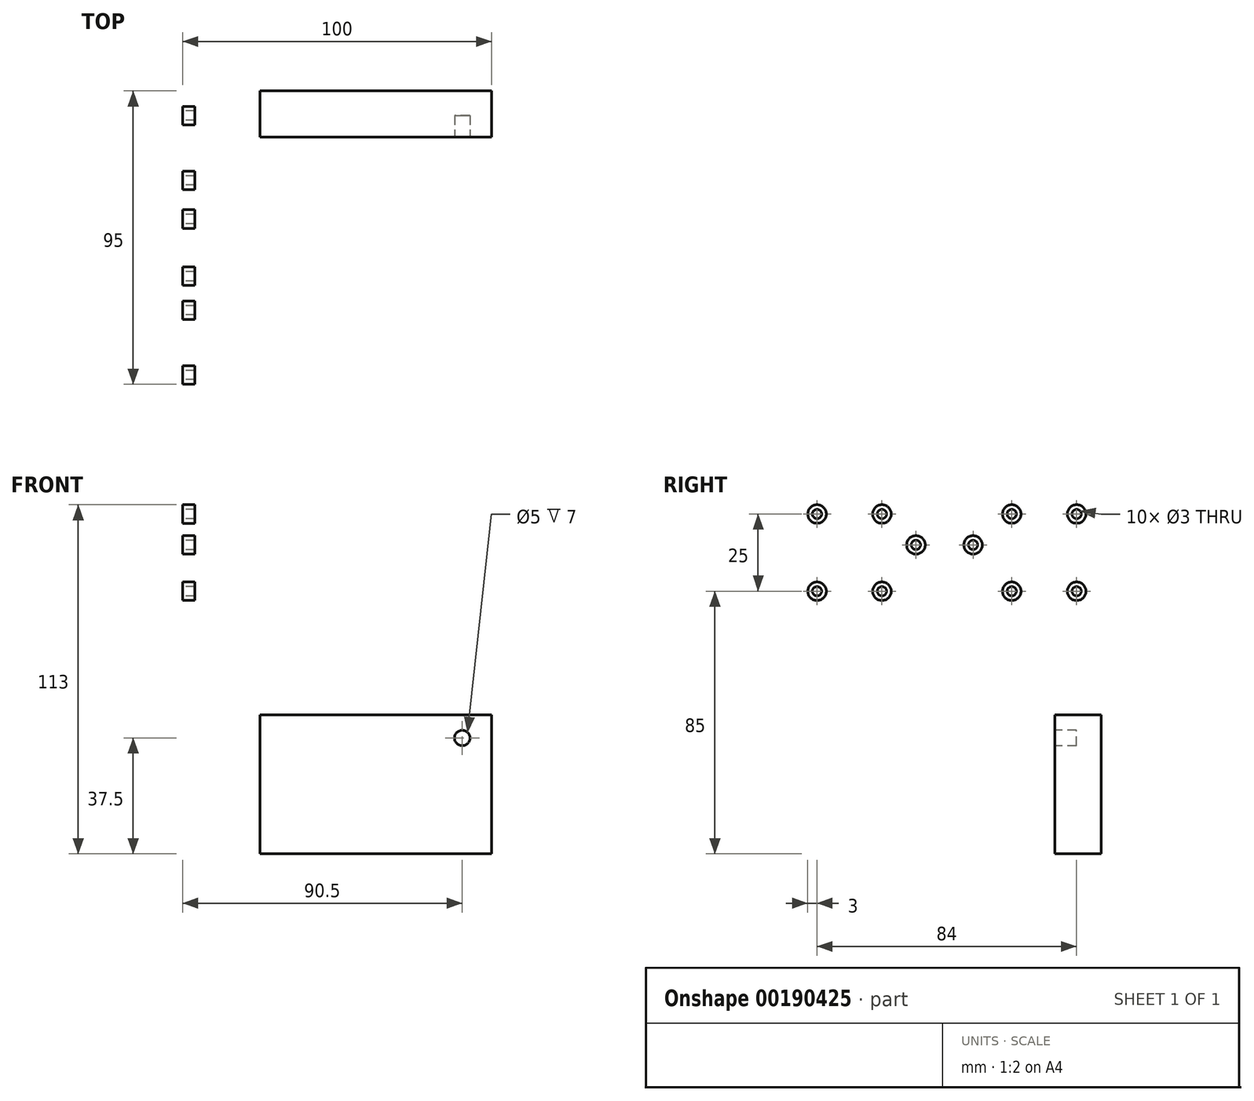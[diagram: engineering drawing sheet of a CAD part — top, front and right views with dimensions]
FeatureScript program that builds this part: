
annotation { "Feature Type Name" : "Feature", "Feature Type Description" : "" }
export const myFeature = defineFeature(function(context is Context, id is Id, definition is map)
    precondition{}
    {
        {
            var Q0;
            Q0=qCreatedBy(makeId("Top.planeOp"),FACE);
            var sketch = newSketch(context, id + "F0", { "sketchPlane" : qUnion([Q0])});
            skLineSegment(sketch, "E0.bottom", {"start": v(0, 0) * mm, "end": v(700, 0) * mm, "construction": true});
            skLineSegment(sketch, "E0.top", {"start": v(0, 670) * mm, "end": v(700, 670) * mm, "construction": true});
            skLineSegment(sketch, "E0.left", {"start": v(0, 0) * mm, "end": v(0, 670) * mm, "construction": true});
            skLineSegment(sketch, "E0.right", {"start": v(700, 0) * mm, "end": v(700, 670) * mm, "construction": true});
            skLineSegment(sketch, "E1.bottom", {"start": v(50, 50) * mm, "end": v(158, 50) * mm, "construction": true});
            skLineSegment(sketch, "E1.top", {"start": v(50, 150) * mm, "end": v(158, 150) * mm, "construction": true});
            skLineSegment(sketch, "E1.left", {"start": v(50, 50) * mm, "end": v(50, 150) * mm, "construction": true});
            skLineSegment(sketch, "E1.right", {"start": v(158, 50) * mm, "end": v(158, 150) * mm, "construction": true});
            skSolve(sketch);
        }
        {
            var Q0;
            Q0=qCreatedBy(makeId("Top.planeOp"),FACE);
            var sketch = newSketch(context, id + "F1", { "sketchPlane" : qUnion([Q0])});
            skLineSegment(sketch, "E2.bottom", {"start": v(50, 150) * mm, "end": v(158, 150) * mm});
            skLineSegment(sketch, "E2.top", {"start": v(50, 50) * mm, "end": v(158, 50) * mm});
            skLineSegment(sketch, "E2.left", {"start": v(50, 150) * mm, "end": v(50, 50) * mm});
            skLineSegment(sketch, "E2.right", {"start": v(158, 150) * mm, "end": v(158, 50) * mm});
            skCircle(sketch, "E3", {"center": v(104.5, 100) * mm, "radius": 21.5 * mm});
            skPoint(sketch, "E4", {"position": v(158, 100) * mm});
            skLineSegment(sketch, "E5.bottom", {"start": v(158, 99.75) * mm, "end": v(126, 99.75) * mm});
            skLineSegment(sketch, "E5.top", {"start": v(158, 100.25) * mm, "end": v(126, 100.25) * mm});
            skLineSegment(sketch, "E5.left", {"start": v(158, 100.25) * mm, "end": v(158, 99.75) * mm});
            skLineSegment(sketch, "E5.right", {"start": v(126, 100.25) * mm, "end": v(126, 99.75) * mm});
            skPoint(sketch, "E6", {"position": v(126, 100) * mm});
            skLineSegment(sketch, "E7.bottom", {"start": v(126, 100.25) * mm, "end": v(100.94, 100.25) * mm});
            skLineSegment(sketch, "E7.top", {"start": v(126, 99.75) * mm, "end": v(100.94, 99.75) * mm});
            skLineSegment(sketch, "E7.right", {"start": v(100.94, 100.25) * mm, "end": v(100.94, 99.75) * mm});
            skLineSegment(sketch, "E8.bottom", {"start": v(158, 150) * mm, "end": v(83, 150) * mm});
            skLineSegment(sketch, "E8.top", {"start": v(158, 135) * mm, "end": v(83, 135) * mm});
            skLineSegment(sketch, "E8.left", {"start": v(158, 150) * mm, "end": v(158, 135) * mm});
            skLineSegment(sketch, "E8.right", {"start": v(83, 150) * mm, "end": v(83, 135) * mm});
            skLineSegment(sketch, "E9.bottom", {"start": v(158, 50) * mm, "end": v(83, 50) * mm});
            skLineSegment(sketch, "E9.top", {"start": v(158, 65) * mm, "end": v(83, 65) * mm});
            skLineSegment(sketch, "E9.left", {"start": v(158, 50) * mm, "end": v(158, 65) * mm});
            skLineSegment(sketch, "E9.right", {"start": v(83, 50) * mm, "end": v(83, 65) * mm});
            skSolve(sketch);
        }
        {
            var Q0;
            Q0=qCreatedBy(makeId("Front.planeOp"),FACE);
            var sketch = newSketch(context, id + "F2", { "sketchPlane" : qUnion([Q0])});
            skPoint(sketch, "E10", {"position": v(158, 0) * mm});
            skPoint(sketch, "E11", {"position": v(50, 0) * mm});
            skLineSegment(sketch, "E12.bottom", {"start": v(50, 30) * mm, "end": v(158, 30) * mm});
            skLineSegment(sketch, "E12.top", {"start": v(50, 45) * mm, "end": v(158, 45) * mm});
            skLineSegment(sketch, "E12.left", {"start": v(50, 30) * mm, "end": v(50, 45) * mm});
            skLineSegment(sketch, "E12.right", {"start": v(158, 30) * mm, "end": v(158, 45) * mm});
            skLineSegment(sketch, "E13.bottom", {"start": v(50, 45) * mm, "end": v(58, 45) * mm});
            skLineSegment(sketch, "E13.top", {"start": v(50, 225) * mm, "end": v(58, 225) * mm});
            skLineSegment(sketch, "E13.left", {"start": v(50, 45) * mm, "end": v(50, 225) * mm});
            skLineSegment(sketch, "E13.right", {"start": v(58, 45) * mm, "end": v(58, 225) * mm});
            skLineSegment(sketch, "E14.bottom", {"start": v(158, 30) * mm, "end": v(50, 30) * mm});
            skLineSegment(sketch, "E14.top", {"start": v(158, 0) * mm, "end": v(50, 0) * mm});
            skLineSegment(sketch, "E14.left", {"start": v(158, 30) * mm, "end": v(158, 0) * mm});
            skLineSegment(sketch, "E14.right", {"start": v(50, 30) * mm, "end": v(50, 0) * mm});
            skLineSegment(sketch, "E15.bottom", {"start": v(50, 225) * mm, "end": v(158, 225) * mm, "construction": true});
            skLineSegment(sketch, "E15.left", {"start": v(50, 225) * mm, "end": v(50, 45) * mm});
            skLineSegment(sketch, "E15.right", {"start": v(158, 225) * mm, "end": v(158, 45) * mm});
            skLineSegment(sketch, "E16.bottom", {"start": v(50, 225) * mm, "end": v(158, 225) * mm});
            skLineSegment(sketch, "E16.top", {"start": v(50, 295) * mm, "end": v(158, 295) * mm});
            skLineSegment(sketch, "E16.left", {"start": v(50, 225) * mm, "end": v(50, 295) * mm});
            skLineSegment(sketch, "E16.right", {"start": v(158, 225) * mm, "end": v(158, 295) * mm});
            skCircle(sketch, "E17", {"center": v(148.5, 37.5) * mm, "radius": 2.5 * mm});
            skPoint(sketch, "E18", {"position": v(158, 37.5) * mm});
            skSolve(sketch);
        }
        {
            var Q0;
            {var subQ1=sQuery(id+"F1.wireOp",EDGE,"E2.bottom");Q0=makeQuery(id+"F1.imprint","IMPRINT",FACE,{"disambiguationData":[TD([[makeQuery(id+"F1.imprint","IMPRINT",EDGE,{"derivedFrom":subQ1}),-1.0]])]});}
            extrude(context, id + "F3", {"entities" : qUnion([Q0]), "depth" : 230 * mm});
        }
        {
            var Q0;
            Q0=makeQuery(id+"F2.imprint","IMPRINT",FACE,{"disambiguationData":[TD([[makeQuery(id+"F2.imprint","IMPRINT",EDGE,{"derivedFrom":sQuery(id+"F2.wireOp",EDGE,"E14.bottom")}),1.0]])]});
            var Q1;
            {var subQ0=sQuery(id+"F2.wireOp",EDGE,"E13.right");Q1=makeQuery(id+"F2.imprint","IMPRINT",FACE,{"disambiguationData":[TD([[makeQuery(id+"F2.imprint","IMPRINT",EDGE,{"derivedFrom":subQ0}),-1.0]])]});}
            var Q2;
            Q2=makeQuery(id+"F2.imprint","IMPRINT",FACE,{"disambiguationData":[TD([[makeQuery(id+"F2.imprint","IMPRINT",EDGE,{"derivedFrom":sQuery(id+"F2.wireOp",EDGE,"E16.top")}),-1.0]])]});
            extrude(context, id + "F4", {"entities" : qUnion([Q0, Q1, Q2]), "operationType" : NewBodyOperationType.REMOVE, "oppositeDirection" : true, "depth" : 310 * mm});
        }
        {
            var Q0;
            Q0=qCreatedBy(makeId("Right.planeOp"),FACE);
            var sketch = newSketch(context, id + "F5", { "sketchPlane" : qUnion([Q0])});
            skCircle(sketch, "E19", {"center": v(142, 85) * mm, "radius": 1.5 * mm});
            skCircle(sketch, "E20", {"center": v(58, 85) * mm, "radius": 1.5 * mm});
            skCircle(sketch, "E21", {"center": v(142, 110) * mm, "radius": 1.5 * mm});
            skCircle(sketch, "E22", {"center": v(58, 110) * mm, "radius": 1.5 * mm});
            skCircle(sketch, "E23", {"center": v(121, 110) * mm, "radius": 1.5 * mm});
            skCircle(sketch, "E24", {"center": v(121, 85) * mm, "radius": 1.5 * mm});
            skCircle(sketch, "E25", {"center": v(79, 110) * mm, "radius": 1.5 * mm});
            skCircle(sketch, "E26", {"center": v(79, 85) * mm, "radius": 1.5 * mm});
            skCircle(sketch, "E27", {"center": v(108.5, 100) * mm, "radius": 1.5 * mm});
            skCircle(sketch, "E28", {"center": v(90, 100) * mm, "radius": 1.5 * mm});
            skCircle(sketch, "E29", {"center": v(58, 110) * mm, "radius": 3 * mm});
            skCircle(sketch, "E30", {"center": v(79, 110) * mm, "radius": 3 * mm});
            skCircle(sketch, "E31", {"center": v(90, 100) * mm, "radius": 3 * mm});
            skCircle(sketch, "E32", {"center": v(108.5, 100) * mm, "radius": 3 * mm});
            skCircle(sketch, "E33", {"center": v(121, 110) * mm, "radius": 3 * mm});
            skCircle(sketch, "E34", {"center": v(142, 110) * mm, "radius": 3 * mm});
            skCircle(sketch, "E35", {"center": v(121, 85) * mm, "radius": 3 * mm});
            skCircle(sketch, "E36", {"center": v(142, 85) * mm, "radius": 3 * mm});
            skCircle(sketch, "E37", {"center": v(79, 85) * mm, "radius": 3 * mm});
            skCircle(sketch, "E38", {"center": v(58, 85) * mm, "radius": 3 * mm});
            skSolve(sketch);
        }
        {
            var Q0;
            Q0=makeQuery(id+"F5.imprint","IMPRINT",FACE,{"disambiguationData":[TD([[makeQuery(id+"F5.imprint","IMPRINT",EDGE,{"derivedFrom":sQuery(id+"F5.wireOp",EDGE,"E19")}),1.0]])]});
            var Q1;
            Q1=makeQuery(id+"F5.imprint","IMPRINT",FACE,{"disambiguationData":[TD([[makeQuery(id+"F5.imprint","IMPRINT",EDGE,{"derivedFrom":sQuery(id+"F5.wireOp",EDGE,"E21")}),1.0]])]});
            var Q2;
            Q2=makeQuery(id+"F5.imprint","IMPRINT",FACE,{"disambiguationData":[TD([[makeQuery(id+"F5.imprint","IMPRINT",EDGE,{"derivedFrom":sQuery(id+"F5.wireOp",EDGE,"E23")}),1.0]])]});
            var Q3;
            Q3=makeQuery(id+"F5.imprint","IMPRINT",FACE,{"disambiguationData":[TD([[makeQuery(id+"F5.imprint","IMPRINT",EDGE,{"derivedFrom":sQuery(id+"F5.wireOp",EDGE,"E27")}),1.0]])]});
            var Q4;
            Q4=makeQuery(id+"F5.imprint","IMPRINT",FACE,{"disambiguationData":[TD([[makeQuery(id+"F5.imprint","IMPRINT",EDGE,{"derivedFrom":sQuery(id+"F5.wireOp",EDGE,"E24")}),1.0]])]});
            var Q5;
            Q5=makeQuery(id+"F5.imprint","IMPRINT",FACE,{"disambiguationData":[TD([[makeQuery(id+"F5.imprint","IMPRINT",EDGE,{"derivedFrom":sQuery(id+"F5.wireOp",EDGE,"E28")}),1.0]])]});
            var Q6;
            Q6=makeQuery(id+"F5.imprint","IMPRINT",FACE,{"disambiguationData":[TD([[makeQuery(id+"F5.imprint","IMPRINT",EDGE,{"derivedFrom":sQuery(id+"F5.wireOp",EDGE,"E26")}),1.0]])]});
            var Q7;
            Q7=makeQuery(id+"F5.imprint","IMPRINT",FACE,{"disambiguationData":[TD([[makeQuery(id+"F5.imprint","IMPRINT",EDGE,{"derivedFrom":sQuery(id+"F5.wireOp",EDGE,"E22")}),1.0]])]});
            var Q8;
            Q8=makeQuery(id+"F5.imprint","IMPRINT",FACE,{"disambiguationData":[TD([[makeQuery(id+"F5.imprint","IMPRINT",EDGE,{"derivedFrom":sQuery(id+"F5.wireOp",EDGE,"E25")}),1.0]])]});
            var Q9;
            Q9=makeQuery(id+"F5.imprint","IMPRINT",FACE,{"disambiguationData":[TD([[makeQuery(id+"F5.imprint","IMPRINT",EDGE,{"derivedFrom":sQuery(id+"F5.wireOp",EDGE,"E20")}),1.0]])]});
            extrude(context, id + "F6", {"entities" : qUnion([Q0, Q1, Q2, Q3, Q4, Q5, Q6, Q7, Q8, Q9]), "operationType" : NewBodyOperationType.REMOVE, "depth" : 71 * mm, "hasSecondDirection" : true, "secondDirectionOppositeDirection" : false, "secondDirectionDepth" : 35 * mm});
        }
        {
            var Q0;
            Q0=makeQuery(id+"F5.imprint","IMPRINT",FACE,{"disambiguationData":[TD([[makeQuery(id+"F5.imprint","IMPRINT",EDGE,{"derivedFrom":sQuery(id+"F5.wireOp",EDGE,"E22")}),-1.0]])]});
            var Q1;
            Q1=makeQuery(id+"F5.imprint","IMPRINT",FACE,{"disambiguationData":[TD([[makeQuery(id+"F5.imprint","IMPRINT",EDGE,{"derivedFrom":sQuery(id+"F5.wireOp",EDGE,"E25")}),-1.0]])]});
            var Q2;
            Q2=makeQuery(id+"F5.imprint","IMPRINT",FACE,{"disambiguationData":[TD([[makeQuery(id+"F5.imprint","IMPRINT",EDGE,{"derivedFrom":sQuery(id+"F5.wireOp",EDGE,"E28")}),-1.0]])]});
            var Q3;
            Q3=makeQuery(id+"F5.imprint","IMPRINT",FACE,{"disambiguationData":[TD([[makeQuery(id+"F5.imprint","IMPRINT",EDGE,{"derivedFrom":sQuery(id+"F5.wireOp",EDGE,"E27")}),-1.0]])]});
            var Q4;
            Q4=makeQuery(id+"F5.imprint","IMPRINT",FACE,{"disambiguationData":[TD([[makeQuery(id+"F5.imprint","IMPRINT",EDGE,{"derivedFrom":sQuery(id+"F5.wireOp",EDGE,"E23")}),-1.0]])]});
            var Q5;
            Q5=makeQuery(id+"F5.imprint","IMPRINT",FACE,{"disambiguationData":[TD([[makeQuery(id+"F5.imprint","IMPRINT",EDGE,{"derivedFrom":sQuery(id+"F5.wireOp",EDGE,"E21")}),-1.0]])]});
            var Q6;
            Q6=makeQuery(id+"F5.imprint","IMPRINT",FACE,{"disambiguationData":[TD([[makeQuery(id+"F5.imprint","IMPRINT",EDGE,{"derivedFrom":sQuery(id+"F5.wireOp",EDGE,"E24")}),-1.0]])]});
            var Q7;
            Q7=makeQuery(id+"F5.imprint","IMPRINT",FACE,{"disambiguationData":[TD([[makeQuery(id+"F5.imprint","IMPRINT",EDGE,{"derivedFrom":sQuery(id+"F5.wireOp",EDGE,"E19")}),-1.0]])]});
            var Q8;
            Q8=makeQuery(id+"F5.imprint","IMPRINT",FACE,{"disambiguationData":[TD([[makeQuery(id+"F5.imprint","IMPRINT",EDGE,{"derivedFrom":sQuery(id+"F5.wireOp",EDGE,"E26")}),-1.0]])]});
            var Q9;
            Q9=makeQuery(id+"F5.imprint","IMPRINT",FACE,{"disambiguationData":[TD([[makeQuery(id+"F5.imprint","IMPRINT",EDGE,{"derivedFrom":sQuery(id+"F5.wireOp",EDGE,"E20")}),-1.0]])]});
            extrude(context, id + "F7", {"entities" : qUnion([Q0, Q1, Q2, Q3, Q4, Q5, Q6, Q7, Q8, Q9]), "operationType" : NewBodyOperationType.ADD, "depth" : 62 * mm, "hasSecondDirection" : true, "secondDirectionOppositeDirection" : false, "secondDirectionDepth" : 58 * mm});
        }
        {
            var Q0;
            Q0=makeQuery(id+"F2.imprint","IMPRINT",FACE,{"disambiguationData":[TD([[makeQuery(id+"F2.imprint","IMPRINT",EDGE,{"derivedFrom":sQuery(id+"F2.wireOp",EDGE,"E17")}),1.0]])]});
            extrude(context, id + "F8", {"entities" : qUnion([Q0]), "operationType" : NewBodyOperationType.REMOVE, "oppositeDirection" : true, "depth" : 142 * mm, "hasSecondDirection" : true, "secondDirectionOppositeDirection" : true, "secondDirectionDepth" : 44 * mm});
        }
    });
